# Revit family: ASH_Contour21_S6481_BIM_DE
name_source: partatom
category: Air Terminals
revit_build: Autodesk Revit 2015 (Build: 20140606_1530(x64)
units: mm (PartAtom-declared; Revit-internal decimal feet)

## types (1)
- S6481LJ - CONTOUR 21 BCKREST 40X17 BLUE NO CUSHION
    Accessories = www.idealspec.co.uk
    AreaUnits = millimeters
    Assembly Code = C1030200
    AssetType = Fixed
    BarCode = 5017830385158
    Brand = Ideal Standard
    Color = Grey
    ConnectionType = Plumbing
    Cost = 0 $
    Description = CONTOUR 21 BCKREST 40X17 BLUE NO CUSHION
    DurationUnit = year
    Finish = Grey
    Help = www.idealstandard.de
    IfcExportAs = IfcSanitaryTerminalType
    IfcExportType = GRABS & HANDLES
    InstallationInstructions = www.idealstandard.de
    LinearUnits = millimeters
    MainColor = Grey
    MaintenanceInformation = www.idealstandard.de
    Manufacturer = www.idealstandard.de
    ManufacturerURL = www.idealstandard.de
    Model = S6481LJ
    ModelNumber = S6481LJ
    ModelReference = CONTOUR 21 BCKREST 40X17 BLUE NO CUSHION
    NettWeight = 0,85 KG
    NominalDepth = 540 mm
    NominalHeight = 90 mm
    NominalLength = 540 mm
    NominalWidth = 95 mm
    ProductInformation = www.idealstandard.de
    Shape = Sculptured
    Size = 90 x 540 x 95 mm
    Space = Internal
    SpareParts = www.idealstandard.de
    URL = www.idealstandard.de

## geometry (parser evidence)
native form markers: Blend x4
no freeform markers — native parametric forms only
